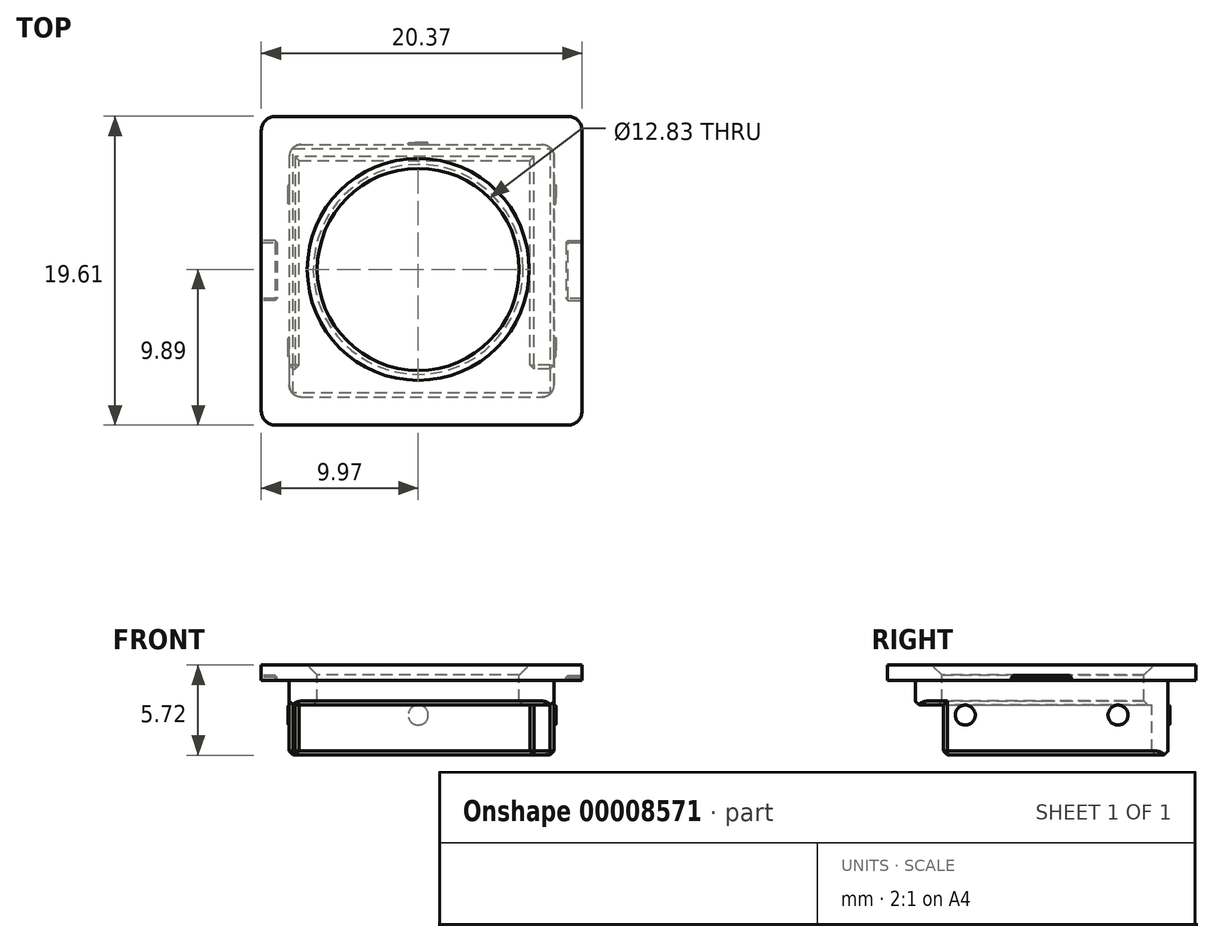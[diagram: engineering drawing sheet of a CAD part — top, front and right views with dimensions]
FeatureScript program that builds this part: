
annotation { "Feature Type Name" : "Feature", "Feature Type Description" : "" }
export const myFeature = defineFeature(function(context is Context, id is Id, definition is map)
    precondition{}
    {
        {
            var Q0;
            Q0=qCreatedBy(makeId("Top.planeOp"),FACE);
            var sketch = newSketch(context, id + "F0", { "sketchPlane" : qUnion([Q0])});
            skLineSegment(sketch, "E0.bottom", {"start": v(-8.2, 7.94) * mm, "end": v(8.62, 7.94) * mm});
            skLineSegment(sketch, "E0.top", {"start": v(-8.2, -8.12) * mm, "end": v(8.62, -8.12) * mm});
            skLineSegment(sketch, "E0.left", {"start": v(-8.2, 7.94) * mm, "end": v(-8.2, -8.12) * mm});
            skLineSegment(sketch, "E0.right", {"start": v(8.62, 7.94) * mm, "end": v(8.62, -8.12) * mm});
            skCircle(sketch, "E1", {"center": v(0, 0) * mm, "radius": 6.41 * mm});
            skLineSegment(sketch, "E2.bottom", {"start": v(10.4, 9.72) * mm, "end": v(-9.97, 9.72) * mm});
            skLineSegment(sketch, "E2.top", {"start": v(10.4, -9.9) * mm, "end": v(-9.97, -9.9) * mm});
            skLineSegment(sketch, "E2.left", {"start": v(10.4, 9.72) * mm, "end": v(10.4, -9.9) * mm});
            skLineSegment(sketch, "E2.right", {"start": v(-9.97, 9.72) * mm, "end": v(-9.97, -9.9) * mm});
            skSolve(sketch);
        }
        {
            var Q0;
            Q0=makeQuery(id+"F0.imprint","IMPRINT",FACE,{"disambiguationData":[TD([[makeQuery(id+"F0.imprint","IMPRINT",EDGE,{"derivedFrom":sQuery(id+"F0.wireOp",EDGE,"E0.bottom")}),-1.0]])]});
            extrude(context, id + "F1", {"entities" : qUnion([Q0]), "oppositeDirection" : true, "depth" : 2.54 * mm});
        }
        {
            var Q0;
            Q0 = qSketchRegion(id + "F0", true);
            extrude(context, id + "F2", {"entities" : qUnion([Q0]), "operationType" : NewBodyOperationType.ADD, "oppositeDirection" : true, "depth" : 0.97 * mm});
        }
        {
            var Q0;
            Q0=makeQuery(id+"F1.opExtrude","CAP_FACE",FACE,{"disambiguationData":[OSD([sQuery(id+"F0.wireOp",EDGE,"E0.bottom"),sQuery(id+"F0.wireOp",EDGE,"E0.top"),sQuery(id+"F0.wireOp",EDGE,"E0.left"),sQuery(id+"F0.wireOp",EDGE,"E0.right"),sQuery(id+"F0.wireOp",EDGE,"E1")])],"isStart":false});
            var sketch = newSketch(context, id + "F3", { "sketchPlane" : qUnion([Q0])});
            skLineSegment(sketch, "E3.bottom", {"start": v(8.62, 6.34) * mm, "end": v(7.1, 6.34) * mm});
            skLineSegment(sketch, "E3.top", {"start": v(8.62, -7.94) * mm, "end": v(7.1, -7.94) * mm});
            skLineSegment(sketch, "E3.left", {"start": v(8.62, 6.34) * mm, "end": v(8.62, -7.94) * mm});
            skLineSegment(sketch, "E3.right", {"start": v(7.1, 6.34) * mm, "end": v(7.1, -6.92) * mm});
            skLineSegment(sketch, "E4.bottom", {"start": v(-8.2, 6.34) * mm, "end": v(-7.56, 6.34) * mm});
            skLineSegment(sketch, "E4.top", {"start": v(-8.2, -7.94) * mm, "end": v(-7.56, -7.94) * mm});
            skLineSegment(sketch, "E4.left", {"start": v(-8.2, 6.34) * mm, "end": v(-8.2, -7.94) * mm});
            skLineSegment(sketch, "E4.right", {"start": v(-7.56, 6.34) * mm, "end": v(-7.56, -6.92) * mm});
            skLineSegment(sketch, "E5.bottom", {"start": v(-7.56, -6.92) * mm, "end": v(7.1, -6.92) * mm});
            skLineSegment(sketch, "E5.top", {"start": v(-7.56, -7.94) * mm, "end": v(7.1, -7.94) * mm});
            skSolve(sketch);
        }
        {
            var Q0;
            Q0 = qSketchRegion(id + "F3", true);
            extrude(context, id + "F4", {"entities" : qUnion([Q0]), "operationType" : NewBodyOperationType.ADD, "depth" : 3.17 * mm});
        }
        {
            var Q0;
            Q0=makeQuery(id+"F4.boolean.opBoolean","MERGE",FACE,{"derivedFrom":[makeQuery(id+"F1.opExtrude","SWEPT_FACE",FACE,{"disambiguationData":[OSD([sQuery(id+"F0.wireOp",EDGE,"E0.left")])]}),makeQuery(id+"F4.opExtrude","SWEPT_FACE",FACE,{"disambiguationData":[OSD([sQuery(id+"F3.wireOp",EDGE,"E4.left")])]})]});
            var sketch = newSketch(context, id + "F5", { "sketchPlane" : qUnion([Q0])});
            skCircle(sketch, "E6", {"center": v(4.94, -3.18) * mm, "radius": 0.64 * mm});
            skPoint(sketch, "E7", {"position": v(-7.94, -0.97) * mm});
            skPoint(sketch, "E8", {"position": v(8.12, -0.97) * mm});
            skPoint(sketch, "E9", {"position": v(-29.26, 19.42) * mm});
            skCircle(sketch, "E10", {"center": v(-4.76, -3.18) * mm, "radius": 0.64 * mm});
            skSolve(sketch);
        }
        {
            var Q0;
            Q0 = qSketchRegion(id + "F5", true);
            extrude(context, id + "F6", {"entities" : qUnion([Q0]), "operationType" : NewBodyOperationType.ADD, "depth" : 0.08 * mm});
        }
        {
            var Q0;
            Q0=makeQuery(id+"F4.boolean.opBoolean","MERGE",FACE,{"derivedFrom":[makeQuery(id+"F1.opExtrude","SWEPT_FACE",FACE,{"disambiguationData":[OSD([sQuery(id+"F0.wireOp",EDGE,"E0.bottom")])]}),makeQuery(id+"F4.opExtrude","SWEPT_FACE",FACE,{"disambiguationData":[OSD([sQuery(id+"F3.wireOp",EDGE,"E3.top"),sQuery(id+"F3.wireOp",EDGE,"E4.top"),sQuery(id+"F3.wireOp",EDGE,"E5.top")])]})]});
            var sketch = newSketch(context, id + "F7", { "sketchPlane" : qUnion([Q0])});
            skCircle(sketch, "E11", {"center": v(0, -3.18) * mm, "radius": 0.64 * mm});
            skSolve(sketch);
        }
        {
            var Q0;
            Q0=makeQuery(id+"F4.boolean.opBoolean","MERGE",FACE,{"derivedFrom":[makeQuery(id+"F1.opExtrude","SWEPT_FACE",FACE,{"disambiguationData":[OSD([sQuery(id+"F0.wireOp",EDGE,"E0.right")])]}),makeQuery(id+"F4.opExtrude","SWEPT_FACE",FACE,{"disambiguationData":[OSD([sQuery(id+"F3.wireOp",EDGE,"E3.left")])]})]});
            var sketch = newSketch(context, id + "F8", { "sketchPlane" : qUnion([Q0])});
            skCircle(sketch, "E12", {"center": v(4.76, -3.18) * mm, "radius": 0.64 * mm});
            skCircle(sketch, "E13", {"center": v(-4.94, -3.18) * mm, "radius": 0.64 * mm});
            skSolve(sketch);
        }
        {
            var Q0;
            Q0=makeQuery(id+"F8.imprint","IMPRINT",FACE,{"disambiguationData":[TD([[makeQuery(id+"F8.imprint","IMPRINT",EDGE,{"derivedFrom":sQuery(id+"F8.wireOp",EDGE,"E12")}),1.0]])]});
            var Q1;
            Q1=makeQuery(id+"F8.imprint","IMPRINT",FACE,{"disambiguationData":[TD([[makeQuery(id+"F8.imprint","IMPRINT",EDGE,{"derivedFrom":sQuery(id+"F8.wireOp",EDGE,"E13")}),1.0]])]});
            extrude(context, id + "F9", {"entities" : qUnion([Q0, Q1]), "operationType" : NewBodyOperationType.ADD, "depth" : 0.13 * mm});
        }
        {
            var Q0;
            Q0 = qSketchRegion(id + "F7", true);
            extrude(context, id + "F10", {"entities" : qUnion([Q0]), "operationType" : NewBodyOperationType.ADD, "depth" : 0.13 * mm});
        }
        {
            var Q0;
            Q0=makeQuery(id+"F6.opExtrude","CAP_EDGE",EDGE,{"disambiguationData":[OSD([sQuery(id+"F5.wireOp",EDGE,"E6")])],"isStart":false});
            var Q1;
            Q1=makeQuery(id+"F9.opExtrude","CAP_EDGE",EDGE,{"disambiguationData":[OSD([sQuery(id+"F8.wireOp",EDGE,"E12")])],"isStart":false});
            var Q2;
            Q2=makeQuery(id+"F6.opExtrude","CAP_EDGE",EDGE,{"disambiguationData":[OSD([sQuery(id+"F5.wireOp",EDGE,"E10")])],"isStart":false});
            var Q3;
            Q3=makeQuery(id+"F9.opExtrude","CAP_EDGE",EDGE,{"disambiguationData":[OSD([sQuery(id+"F8.wireOp",EDGE,"E13")])],"isStart":false});
            var Q4;
            Q4=makeQuery(id+"F10.opExtrude","CAP_EDGE",EDGE,{"disambiguationData":[OSD([sQuery(id+"F7.wireOp",EDGE,"E11")])],"isStart":false});
            fillet(context, id + "F11", {"entities" : qUnion([Q0, Q1, Q2, Q3, Q4]), "radius" : 0.1 * mm, "tangentPropagation" : true, "allowEdgeOverflow" : false});
        }
        {
            var Q0;
            Q0=makeQuery(id+"F2.opExtrude","SWEPT_EDGE",EDGE,{"disambiguationData":[OSD([sQuery(id+"F0.wireOp",EDGE,"E2.bottom"),sQuery(id+"F0.wireOp",EDGE,"E2.right")])]});
            var Q1;
            Q1=makeQuery(id+"F2.opExtrude","SWEPT_EDGE",EDGE,{"disambiguationData":[OSD([sQuery(id+"F0.wireOp",EDGE,"E2.bottom"),sQuery(id+"F0.wireOp",EDGE,"E2.left")])]});
            var Q2;
            Q2=makeQuery(id+"F2.opExtrude","SWEPT_EDGE",EDGE,{"disambiguationData":[OSD([sQuery(id+"F0.wireOp",EDGE,"E2.top"),sQuery(id+"F0.wireOp",EDGE,"E2.left")])]});
            var Q3;
            Q3=makeQuery(id+"F2.opExtrude","SWEPT_EDGE",EDGE,{"disambiguationData":[OSD([sQuery(id+"F0.wireOp",EDGE,"E2.top"),sQuery(id+"F0.wireOp",EDGE,"E2.right")])]});
            fillet(context, id + "F12", {"entities" : qUnion([Q0, Q1, Q2, Q3]), "radius" : 0.89 * mm, "tangentPropagation" : true, "allowEdgeOverflow" : false});
        }
        {
            var Q0;
            Q0=makeQuery(id+"F4.opExtrude","CAP_EDGE",EDGE,{"disambiguationData":[OSD([sQuery(id+"F3.wireOp",EDGE,"E3.top"),sQuery(id+"F3.wireOp",EDGE,"E4.top"),sQuery(id+"F3.wireOp",EDGE,"E5.top")])],"isStart":false});
            var Q1;
            Q1=makeQuery(id+"F4.opExtrude","CAP_EDGE",EDGE,{"disambiguationData":[OSD([sQuery(id+"F3.wireOp",EDGE,"E3.bottom")])],"isStart":false});
            var Q2;
            Q2=makeQuery(id+"F4.opExtrude","CAP_EDGE",EDGE,{"disambiguationData":[OSD([sQuery(id+"F3.wireOp",EDGE,"E3.left")])],"isStart":false});
            var Q3;
            Q3=makeQuery(id+"F4.opExtrude","SWEPT_EDGE",EDGE,{"disambiguationData":[OSD([sQuery(id+"F0.wireOp",EDGE,"E0.right"),sQuery(id+"F3.wireOp",EDGE,"E3.bottom"),sQuery(id+"F3.wireOp",EDGE,"E3.left")])]});
            var Q4;
            Q4=makeQuery(id+"F1.opExtrude","CAP_EDGE",EDGE,{"disambiguationData":[OSD([sQuery(id+"F0.wireOp",EDGE,"E0.right")])],"isStart":false});
            var Q5;
            Q5=makeQuery(id+"F1.opExtrude","CAP_EDGE",EDGE,{"disambiguationData":[OSD([sQuery(id+"F0.wireOp",EDGE,"E0.top")])],"isStart":false});
            var Q6;
            Q6=makeQuery(id+"F1.opExtrude","CAP_EDGE",EDGE,{"disambiguationData":[OSD([sQuery(id+"F0.wireOp",EDGE,"E0.left")])],"isStart":false});
            var Q7;
            Q7=makeQuery(id+"F4.opExtrude","SWEPT_EDGE",EDGE,{"disambiguationData":[OSD([sQuery(id+"F0.wireOp",EDGE,"E0.left"),sQuery(id+"F3.wireOp",EDGE,"E4.bottom"),sQuery(id+"F3.wireOp",EDGE,"E4.left")])]});
            var Q8;
            Q8=makeQuery(id+"F4.opExtrude","CAP_EDGE",EDGE,{"disambiguationData":[OSD([sQuery(id+"F3.wireOp",EDGE,"E4.left")])],"isStart":false});
            var Q9;
            Q9=makeQuery(id+"F4.opExtrude","CAP_EDGE",EDGE,{"disambiguationData":[OSD([sQuery(id+"F3.wireOp",EDGE,"E4.bottom")])],"isStart":false});
            var Q10;
            Q10=makeQuery(id+"F4.opExtrude","CAP_EDGE",EDGE,{"disambiguationData":[OSD([sQuery(id+"F3.wireOp",EDGE,"E3.right")])],"isStart":false});
            var Q11;
            Q11=makeQuery(id+"F4.opExtrude","CAP_EDGE",EDGE,{"disambiguationData":[OSD([sQuery(id+"F3.wireOp",EDGE,"E5.bottom")])],"isStart":false});
            var Q12;
            Q12=makeQuery(id+"F4.opExtrude","CAP_EDGE",EDGE,{"disambiguationData":[OSD([sQuery(id+"F3.wireOp",EDGE,"E4.right")])],"isStart":false});
            var Q13;
            Q13=makeQuery(id+"F4.opExtrude","SWEPT_EDGE",EDGE,{"disambiguationData":[OSD([sQuery(id+"F3.wireOp",EDGE,"E3.bottom"),sQuery(id+"F3.wireOp",EDGE,"E3.right")])]});
            var Q14;
            Q14=makeQuery(id+"F4.opExtrude","SWEPT_EDGE",EDGE,{"disambiguationData":[OSD([sQuery(id+"F3.wireOp",EDGE,"E4.bottom"),sQuery(id+"F3.wireOp",EDGE,"E4.right")])]});
            var Q15;
            Q15=makeQuery(id+"F1.opExtrude","CAP_EDGE",EDGE,{"disambiguationData":[OSD([sQuery(id+"F0.wireOp",EDGE,"E1")])],"isStart":false});
            chamfer(context, id + "F13", {"entities" : qUnion([Q0, Q1, Q2, Q3, Q4, Q5, Q6, Q7, Q8, Q9, Q10, Q11, Q12, Q13, Q14, Q15]), "width" : 0.25 * mm, "tangentPropagation" : true});
        }
        {
            var Q0;
            Q0=makeQuery(id+"F4.boolean.opBoolean","MERGE",EDGE,{"derivedFrom":[makeQuery(id+"F1.opExtrude","SWEPT_EDGE",EDGE,{"disambiguationData":[OSD([sQuery(id+"F0.wireOp",EDGE,"E0.bottom"),sQuery(id+"F0.wireOp",EDGE,"E0.left")])]}),makeQuery(id+"F4.opExtrude","SWEPT_EDGE",EDGE,{"disambiguationData":[OSD([sQuery(id+"F3.wireOp",EDGE,"E4.top"),sQuery(id+"F3.wireOp",EDGE,"E4.left")])]})]});
            var Q1;
            Q1=makeQuery(id+"F4.boolean.opBoolean","MERGE",EDGE,{"derivedFrom":[makeQuery(id+"F1.opExtrude","SWEPT_EDGE",EDGE,{"disambiguationData":[OSD([sQuery(id+"F0.wireOp",EDGE,"E0.bottom"),sQuery(id+"F0.wireOp",EDGE,"E0.right")])]}),makeQuery(id+"F4.opExtrude","SWEPT_EDGE",EDGE,{"disambiguationData":[OSD([sQuery(id+"F3.wireOp",EDGE,"E3.top"),sQuery(id+"F3.wireOp",EDGE,"E3.left")])]})]});
            var Q2;
            Q2=makeQuery(id+"F1.opExtrude","SWEPT_EDGE",EDGE,{"disambiguationData":[OSD([sQuery(id+"F0.wireOp",EDGE,"E0.top"),sQuery(id+"F0.wireOp",EDGE,"E0.right")])]});
            var Q3;
            Q3=makeQuery(id+"F1.opExtrude","SWEPT_EDGE",EDGE,{"disambiguationData":[OSD([sQuery(id+"F0.wireOp",EDGE,"E0.top"),sQuery(id+"F0.wireOp",EDGE,"E0.left")])]});
            fillet(context, id + "F14", {"entities" : qUnion([Q0, Q1, Q2, Q3]), "radius" : 0.76 * mm, "tangentPropagation" : true, "allowEdgeOverflow" : false});
        }
        {
            var Q0;
            Q0=makeQuery(id+"F2.opExtrude","SWEPT_FACE",FACE,{"disambiguationData":[OSD([sQuery(id+"F0.wireOp",EDGE,"E2.left")])]});
            var sketch = newSketch(context, id + "F15", { "sketchPlane" : qUnion([Q0])});
            skLineSegment(sketch, "E14.bottom", {"start": v(-2, -0.97) * mm, "end": v(1.82, -0.97) * mm});
            skLineSegment(sketch, "E14.top", {"start": v(-2, -0.66) * mm, "end": v(1.82, -0.66) * mm});
            skLineSegment(sketch, "E14.left", {"start": v(-2, -0.97) * mm, "end": v(-2, -0.66) * mm});
            skLineSegment(sketch, "E14.right", {"start": v(1.82, -0.97) * mm, "end": v(1.82, -0.66) * mm});
            skSolve(sketch);
        }
        {
            var Q0;
            Q0 = qSketchRegion(id + "F15", true);
            extrude(context, id + "F16", {"entities" : qUnion([Q0]), "operationType" : NewBodyOperationType.REMOVE, "oppositeDirection" : true, "depth" : 1.02 * mm});
        }
        {
            var Q0;
            Q0=makeQuery(id+"F2.opExtrude","SWEPT_FACE",FACE,{"disambiguationData":[OSD([sQuery(id+"F0.wireOp",EDGE,"E2.right")])]});
            var sketch = newSketch(context, id + "F17", { "sketchPlane" : qUnion([Q0])});
            skLineSegment(sketch, "E15.bottom", {"start": v(-1.82, -0.97) * mm, "end": v(2, -0.97) * mm});
            skLineSegment(sketch, "E15.top", {"start": v(-1.82, -0.66) * mm, "end": v(2, -0.66) * mm});
            skLineSegment(sketch, "E15.left", {"start": v(-1.82, -0.97) * mm, "end": v(-1.82, -0.66) * mm});
            skLineSegment(sketch, "E15.right", {"start": v(2, -0.97) * mm, "end": v(2, -0.66) * mm});
            skSolve(sketch);
        }
        {
            var Q0;
            Q0 = qSketchRegion(id + "F17", true);
            extrude(context, id + "F18", {"entities" : qUnion([Q0]), "operationType" : NewBodyOperationType.REMOVE, "oppositeDirection" : true, "depth" : 1.02 * mm});
        }
        {
            var Q0;
            Q0=makeQuery(id+"F16.boolean.opBoolean","COPY",EDGE,{"derivedFrom":makeQuery(id+"F16.opExtrude","CAP_EDGE",EDGE,{"disambiguationData":[OSD([sQuery(id+"F15.wireOp",EDGE,"E14.right")])],"isStart":true})});
            var Q1;
            Q1=makeQuery(id+"F16.boolean.opBoolean","COPY",EDGE,{"derivedFrom":makeQuery(id+"F16.opExtrude","CAP_EDGE",EDGE,{"disambiguationData":[OSD([sQuery(id+"F15.wireOp",EDGE,"E14.top")])],"isStart":true})});
            var Q2;
            Q2=makeQuery(id+"F16.boolean.opBoolean","COPY",EDGE,{"derivedFrom":makeQuery(id+"F16.opExtrude","CAP_EDGE",EDGE,{"disambiguationData":[OSD([sQuery(id+"F15.wireOp",EDGE,"E14.left")])],"isStart":true})});
            var Q3;
            Q3=makeQuery(id+"F16.boolean.opBoolean","COPY",EDGE,{"derivedFrom":makeQuery(id+"F16.opExtrude","SWEPT_EDGE",EDGE,{"disambiguationData":[OSD([sQuery(id+"F15.wireOp",EDGE,"E14.top"),sQuery(id+"F15.wireOp",EDGE,"E14.left")])]})});
            var Q4;
            Q4=makeQuery(id+"F16.boolean.opBoolean","COPY",EDGE,{"derivedFrom":makeQuery(id+"F16.opExtrude","CAP_EDGE",EDGE,{"disambiguationData":[OSD([sQuery(id+"F15.wireOp",EDGE,"E14.top")])],"isStart":false})});
            var Q5;
            Q5=makeQuery(id+"F16.boolean.opBoolean","COPY",EDGE,{"derivedFrom":makeQuery(id+"F16.opExtrude","SWEPT_EDGE",EDGE,{"disambiguationData":[OSD([sQuery(id+"F15.wireOp",EDGE,"E14.top"),sQuery(id+"F15.wireOp",EDGE,"E14.right")])]})});
            var Q6;
            Q6=makeQuery(id+"F16.boolean.opBoolean","COPY",EDGE,{"derivedFrom":makeQuery(id+"F16.opExtrude","CAP_EDGE",EDGE,{"disambiguationData":[OSD([sQuery(id+"F15.wireOp",EDGE,"E14.right")])],"isStart":false})});
            var Q7;
            Q7=makeQuery(id+"F16.boolean.opBoolean","COPY",EDGE,{"derivedFrom":makeQuery(id+"F16.opExtrude","CAP_EDGE",EDGE,{"disambiguationData":[OSD([sQuery(id+"F15.wireOp",EDGE,"E14.left")])],"isStart":false})});
            var Q8;
            Q8=makeQuery(id+"F18.boolean.opBoolean","COPY",EDGE,{"derivedFrom":makeQuery(id+"F18.opExtrude","CAP_EDGE",EDGE,{"disambiguationData":[OSD([sQuery(id+"F17.wireOp",EDGE,"E15.left")])],"isStart":false})});
            var Q9;
            Q9=makeQuery(id+"F18.boolean.opBoolean","COPY",EDGE,{"derivedFrom":makeQuery(id+"F18.opExtrude","CAP_EDGE",EDGE,{"disambiguationData":[OSD([sQuery(id+"F17.wireOp",EDGE,"E15.top")])],"isStart":false})});
            var Q10;
            Q10=makeQuery(id+"F18.boolean.opBoolean","COPY",EDGE,{"derivedFrom":makeQuery(id+"F18.opExtrude","CAP_EDGE",EDGE,{"disambiguationData":[OSD([sQuery(id+"F17.wireOp",EDGE,"E15.left")])],"isStart":true})});
            var Q11;
            Q11=makeQuery(id+"F18.boolean.opBoolean","COPY",EDGE,{"derivedFrom":makeQuery(id+"F18.opExtrude","CAP_EDGE",EDGE,{"disambiguationData":[OSD([sQuery(id+"F17.wireOp",EDGE,"E15.top")])],"isStart":true})});
            var Q12;
            Q12=makeQuery(id+"F18.boolean.opBoolean","COPY",EDGE,{"derivedFrom":makeQuery(id+"F18.opExtrude","SWEPT_EDGE",EDGE,{"disambiguationData":[OSD([sQuery(id+"F17.wireOp",EDGE,"E15.top"),sQuery(id+"F17.wireOp",EDGE,"E15.left")])]})});
            var Q13;
            Q13=makeQuery(id+"F18.boolean.opBoolean","COPY",EDGE,{"derivedFrom":makeQuery(id+"F18.opExtrude","CAP_EDGE",EDGE,{"disambiguationData":[OSD([sQuery(id+"F17.wireOp",EDGE,"E15.right")])],"isStart":true})});
            var Q14;
            Q14=makeQuery(id+"F18.boolean.opBoolean","COPY",EDGE,{"derivedFrom":makeQuery(id+"F18.opExtrude","CAP_EDGE",EDGE,{"disambiguationData":[OSD([sQuery(id+"F17.wireOp",EDGE,"E15.right")])],"isStart":false})});
            var Q15;
            Q15=makeQuery(id+"F18.boolean.opBoolean","COPY",EDGE,{"derivedFrom":makeQuery(id+"F18.opExtrude","SWEPT_EDGE",EDGE,{"disambiguationData":[OSD([sQuery(id+"F17.wireOp",EDGE,"E15.top"),sQuery(id+"F17.wireOp",EDGE,"E15.right")])]})});
            chamfer(context, id + "F19", {"entities" : qUnion([Q0, Q1, Q2, Q3, Q4, Q5, Q6, Q7, Q8, Q9, Q10, Q11, Q12, Q13, Q14, Q15]), "width" : 0.13 * mm, "tangentPropagation" : true});
        }
        {
            var Q0;
            Q0=makeQuery(id+"F1.opExtrude","CAP_EDGE",EDGE,{"disambiguationData":[OSD([sQuery(id+"F0.wireOp",EDGE,"E1")])],"isStart":true});
            chamfer(context, id + "F20", {"entities" : qUnion([Q0]), "width" : 0.64 * mm, "tangentPropagation" : true});
        }
    });
